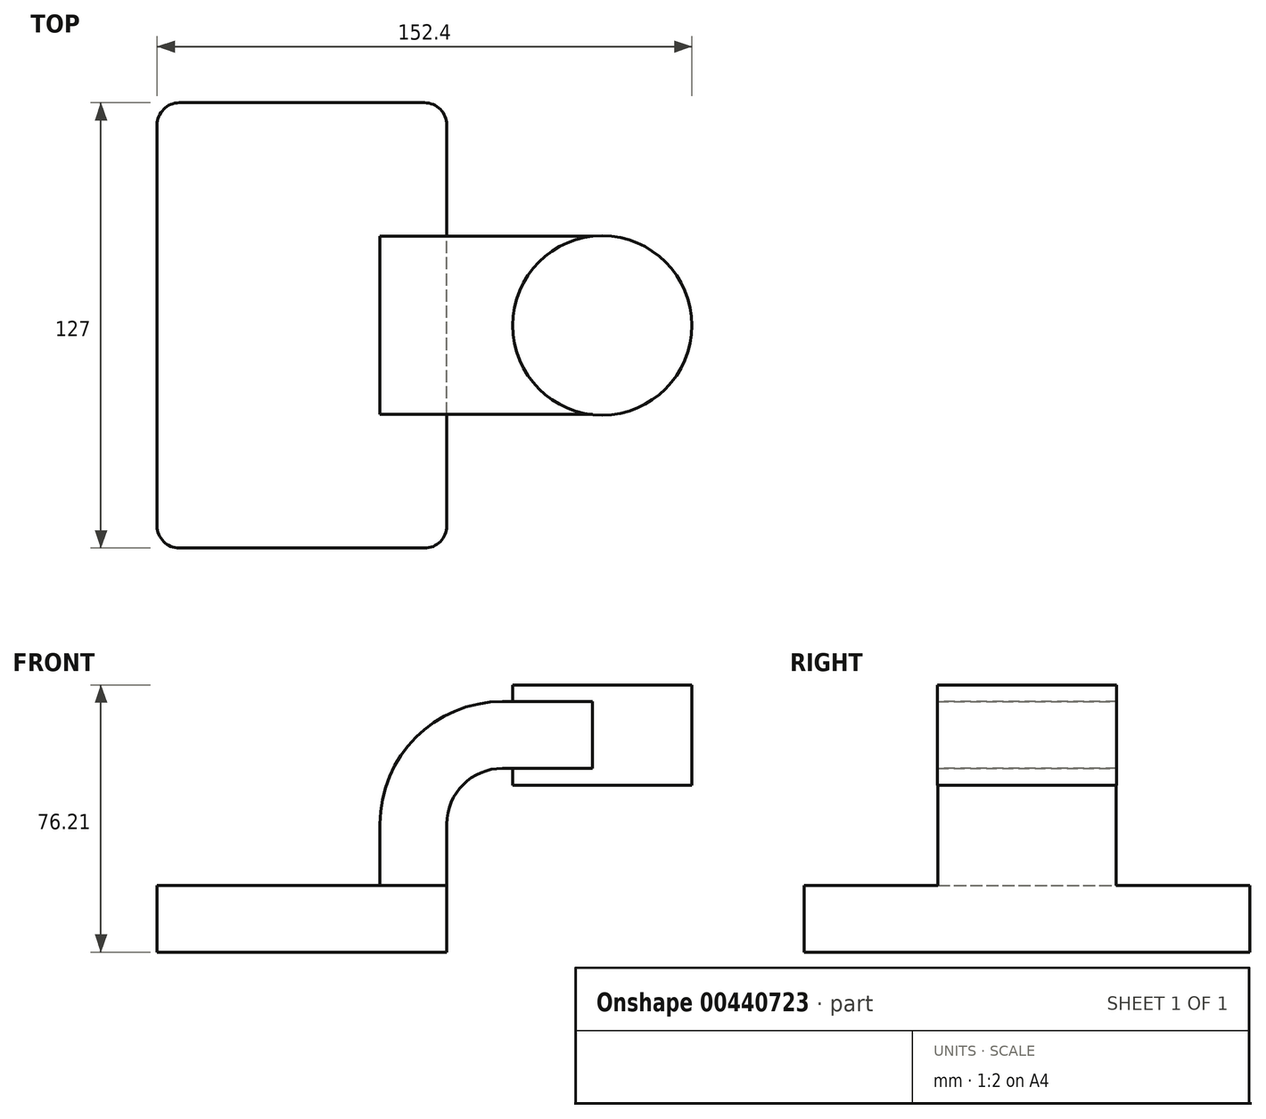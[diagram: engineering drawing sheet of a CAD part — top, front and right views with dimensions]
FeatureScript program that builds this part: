
annotation { "Feature Type Name" : "Feature", "Feature Type Description" : "" }
export const myFeature = defineFeature(function(context is Context, id is Id, definition is map)
    precondition{}
    {
        {
            var Q0;
            Q0=qCreatedBy(makeId("Front.planeOp"),FACE);
            var sketch = newSketch(context, id + "F0", { "sketchPlane" : qUnion([Q0])});
            skLineSegment(sketch, "E0.bottom", {"start": v(-41.27, -9.53) * mm, "end": v(41.28, -9.53) * mm});
            skLineSegment(sketch, "E0.top", {"start": v(-41.28, 9.52) * mm, "end": v(41.28, 9.52) * mm});
            skLineSegment(sketch, "E0.left", {"start": v(-41.28, -9.53) * mm, "end": v(-41.28, 9.53) * mm});
            skLineSegment(sketch, "E0.right", {"start": v(41.28, -9.53) * mm, "end": v(41.28, 9.52) * mm});
            skPoint(sketch, "E0.middle", {"position": v(0, 0) * mm});
            skLineSegment(sketch, "E1.bottom", {"start": v(60.32, 38.1) * mm, "end": v(111.12, 38.1) * mm});
            skLineSegment(sketch, "E1.top", {"start": v(60.32, 66.67) * mm, "end": v(111.12, 66.67) * mm});
            skLineSegment(sketch, "E1.left", {"start": v(60.32, 38.1) * mm, "end": v(60.32, 66.67) * mm});
            skLineSegment(sketch, "E1.right", {"start": v(111.12, 38.1) * mm, "end": v(111.12, 66.67) * mm});
            skPoint(sketch, "E1.middle", {"position": v(85.72, 52.39) * mm});
            skLineSegment(sketch, "E2", {"start": v(41.28, 9.52) * mm, "end": v(41.28, 27) * mm});
            skArc(sketch, "E3", {"start": v(41.27, 27) * mm, "mid": v(45.92, 38.23) * mm, "end": v(57.15, 42.88) * mm});
            skArc(sketch, "E4.1", {"start": v(22.23, 27) * mm, "mid": v(32.45, 51.7) * mm, "end": v(57.15, 61.93) * mm});
            skLineSegment(sketch, "E4.2", {"start": v(22.22, 9.52) * mm, "end": v(22.22, 27) * mm});
            skFitSpline(sketch, "E5", {"points": [v(-41.28, 9.53) * mm, v(57.15, 61.93) * mm], "startDerivative": vector(38.26, 58.9) * mm, "endDerivative": vector(133.54, -1.5) * mm});
            skLineSegment(sketch, "E6", {"start": v(57.15, 42.88) * mm, "end": v(85.57, 42.88) * mm});
            skLineSegment(sketch, "E7.0", {"start": v(57.15, 61.93) * mm, "end": v(85.57, 61.93) * mm});
            skLineSegment(sketch, "E8", {"start": v(85.57, 66.67) * mm, "end": v(85.57, 38.1) * mm});
            skPoint(sketch, "E8.startSnap0", {"position": v(85.72, 66.67) * mm});
            skSolve(sketch);
        }
        {
            var Q0;
            Q0=makeQuery(id+"F0.imprint","IMPRINT",FACE,{"disambiguationData":[TD([[makeQuery(id+"F0.imprint","IMPRINT",EDGE,{"derivedFrom":sQuery(id+"F0.wireOp",EDGE,"E0.bottom")}),1.0]])]});
            extrude(context, id + "F1", {"entities" : qUnion([Q0]), "endBound" : BoundingType.SYMMETRIC, "depth" : 127 * mm});
        }
        {
            var Q0;
            Q0=makeQuery(id+"F0.imprint","IMPRINT",FACE,{"disambiguationData":[TD([[makeQuery(id+"F0.imprint","IMPRINT",EDGE,{"derivedFrom":sQuery(id+"F0.wireOp",EDGE,"E4.1")}),1.0]])]});
            extrude(context, id + "F2", {"entities" : qUnion([Q0]), "operationType" : NewBodyOperationType.ADD, "endBound" : BoundingType.SYMMETRIC, "depth" : 15.88 * mm});
        }
        {
            var Q0;
            {var subQ0=sQuery(id+"F0.wireOp",EDGE,"E2");Q0=makeQuery(id+"F0.imprint","IMPRINT",FACE,{"disambiguationData":[TD([[makeQuery(id+"F0.imprint","IMPRINT",EDGE,{"derivedFrom":subQ0}),1.0]])]});}
            var Q1;
            {var subQ5=sQuery(id+"F0.wireOp",EDGE,"q3Rt58tE-2fDw-KW1H-uc7U-yLOGCJB6ST7r");Q1=makeQuery(id+"F0.imprint","IMPRINT",FACE,{"disambiguationData":[TD([[makeQuery(id+"F0.imprint","IMPRINT",EDGE,{"derivedFrom":subQ5}),-1.0]])]});}
            extrude(context, id + "F3", {"entities" : qUnion([Q0, Q1]), "operationType" : NewBodyOperationType.ADD, "endBound" : BoundingType.SYMMETRIC, "depth" : 50.8 * mm});
        }
        {
            var Q0;
            {var subQ0=sQuery(id+"F0.wireOp",EDGE,"E6");var subQ1=sQuery(id+"F0.wireOp",EDGE,"E1.left");var subQ2=makeQuery(id+"F0.imprint","INTERSECT",VERTEX,{"derivedFrom":[subQ1,subQ0]});Q0=makeQuery(id+"F0.imprint","IMPRINT",FACE,{"disambiguationData":[TD([[makeQuery(id+"F0.imprint","IMPRINT",EDGE,{"disambiguationData":[TD([[subQ2,-1.0]])],"derivedFrom":subQ1}),-1.0]])]});}
            extrude(context, id + "F4", {"entities" : qUnion([Q0]), "operationType" : NewBodyOperationType.ADD, "endBound" : BoundingType.SYMMETRIC, "depth" : 50.8 * mm});
        }
        {
            var Q0;
            {var subQ4=sQuery(id+"F0.wireOp",EDGE,"E1.right");Q0=makeQuery(id+"F0.imprint","IMPRINT",FACE,{"disambiguationData":[TD([[makeQuery(id+"F0.imprint","IMPRINT",EDGE,{"derivedFrom":subQ4}),1.0]])]});}
            var Q1;
            Q1=sQuery(id+"F0.wireOp",EDGE,"E8");
            revolve(context, id + "F5", {"operationType" : NewBodyOperationType.ADD, "entities" : qUnion([Q0]), "axis" : qUnion([Q1]), "revolveType" : RevolveType.FULL});
        }
        {
            var Q0;
            Q0=makeQuery(id+"F1.opExtrude","CAP_EDGE",EDGE,{"disambiguationData":[OSD([sQuery(id+"F0.wireOp",EDGE,"E0.left")])],"isStart":false});
            var Q1;
            Q1=makeQuery(id+"F1.opExtrude","CAP_EDGE",EDGE,{"disambiguationData":[OSD([sQuery(id+"F0.wireOp",EDGE,"E0.right")])],"isStart":false});
            var Q2;
            Q2=makeQuery(id+"F1.opExtrude","CAP_EDGE",EDGE,{"disambiguationData":[OSD([sQuery(id+"F0.wireOp",EDGE,"E0.right")])],"isStart":true});
            var Q3;
            Q3=makeQuery(id+"F1.opExtrude","CAP_EDGE",EDGE,{"disambiguationData":[OSD([sQuery(id+"F0.wireOp",EDGE,"E0.left")])],"isStart":true});
            fillet(context, id + "F6", {"entities" : qUnion([Q0, Q1, Q2, Q3]), "radius" : 6.35 * mm, "tangentPropagation" : true, "allowEdgeOverflow" : false});
        }
    });
